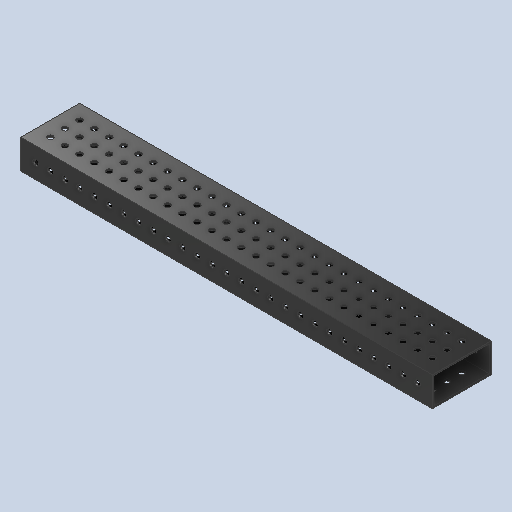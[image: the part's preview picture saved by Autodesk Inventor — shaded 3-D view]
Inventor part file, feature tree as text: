
AUTODESK INVENTOR PART (.ipt)
format: ipt  version: 2024 (Build 280153000, 153)  size: 573,440 bytes
history: native  units: in
note: dims shown in document units (in); Inventor stores cm internally (conversion verified against a paired STEP export)
features: other x4, extrude x1, sketch x1
ambient origin geometry x8: Origin, YZ Plane, XZ Plane, XY Plane, X Axis, Y Axis, Z Axis, Center Point
bodies: Body1 (feature_tree)
feature tree (6):
  other  "2024-220-002-Shootaur-Rest"
  other  "2024-220-000-Hard-Stop.ipt"
  extrude  "Extrusion1"  Depth=0.3937in
  other  "2024-220-002-Shootaur-Rest::2024-220-000-Hard-Stop.ipt"
  other  "TaggingFeature1"
  sketch  "Sketch1"  dims[d0=0.3937in d1=0.196in d2=0.5in d3=0.5in d4=1.1811in d6=0.5in d7=10.6299in d9=0.5in d12=1.1875in d13=0.0in]
